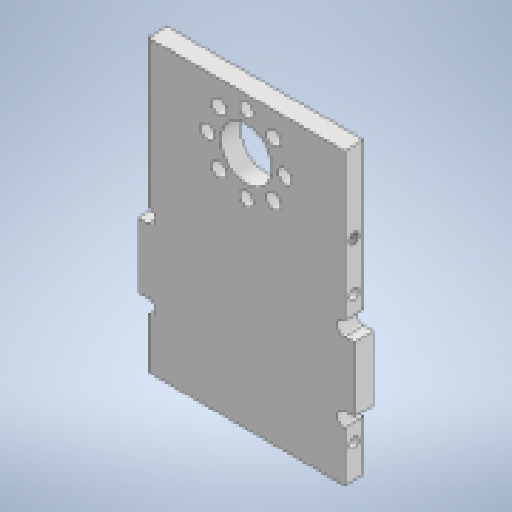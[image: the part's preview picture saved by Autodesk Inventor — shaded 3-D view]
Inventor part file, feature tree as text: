
AUTODESK INVENTOR PART (.ipt)
format: ipt  version: 2025.1 (Build 291241000, 241)  size: 198,144 bytes
history: native  units: mm
features: extrude x4, sketch x4, other x2, hole x1
ambient origin geometry x8: Origin, YZ Plane, XZ Plane, XY Plane, X Axis, Y Axis, Z Axis, Center Point
bodies: Body1 (feature_tree)
feature tree (11):
  other  "ソリッド1"
  extrude  "押し出し1"  Depth=30.5mm
  sketch  "スケッチ2"
  extrude  "押し出し2"  Depth=45.0mm
  extrude  "押し出し3"  Depth=3.0mm TaperAngle=0.0deg
  hole  "穴1"  [1 undecoded]
  extrude  "押し出し4"  Depth=1.5mm
  sketch  "スケッチ1"
  sketch  "スケッチ3"
  sketch  "スケッチ4"
  other  "スケッチ円形状パターン1"
note: 1 required parameter value undecoded (feature->parameter linkage not recoverable at this tier; creation-order binding heuristic only, values carry confidence <= 0.55)
